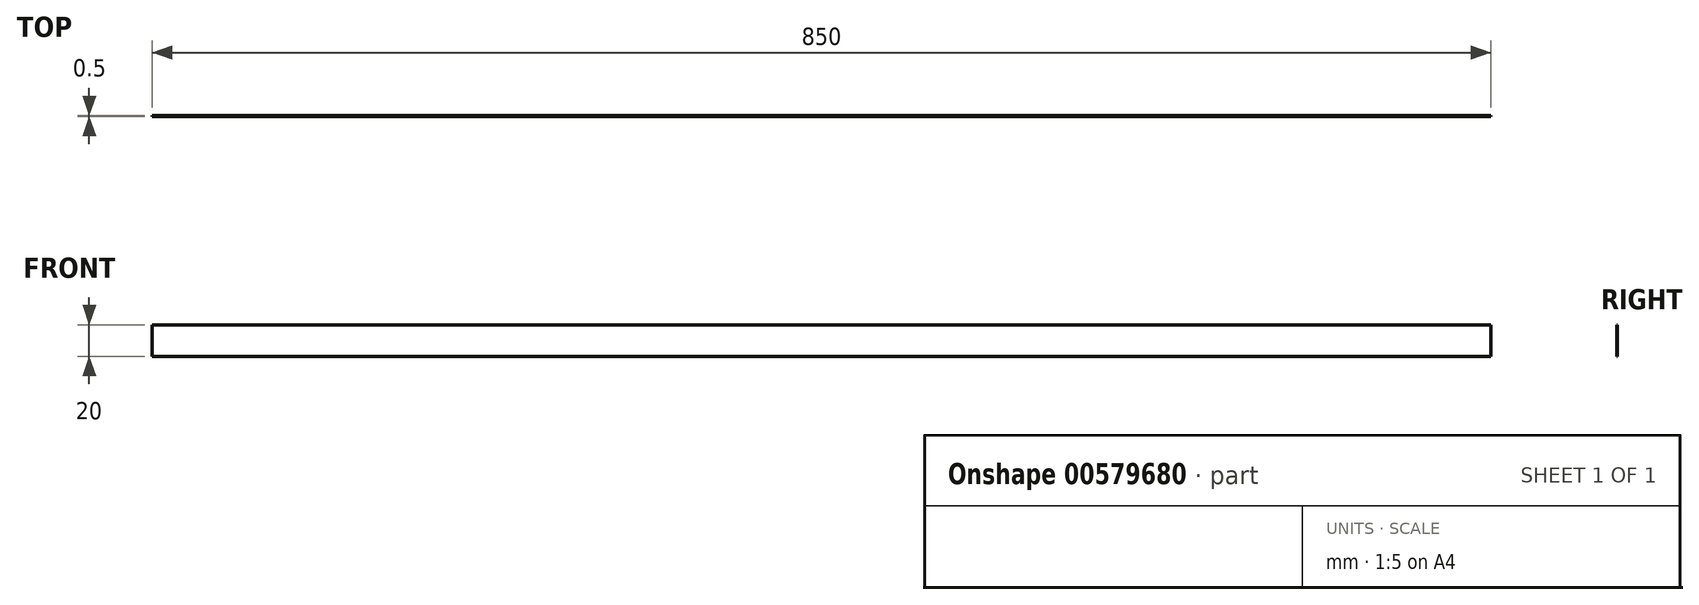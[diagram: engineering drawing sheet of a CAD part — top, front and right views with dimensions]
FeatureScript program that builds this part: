
annotation { "Feature Type Name" : "Feature", "Feature Type Description" : "" }
export const myFeature = defineFeature(function(context is Context, id is Id, definition is map)
    precondition{}
    {
        {
            var Q0;
            Q0=qCreatedBy(makeId("Front.planeOp"),FACE);
            var sketch = newSketch(context, id + "F0", { "sketchPlane" : qUnion([Q0])});
            skLineSegment(sketch, "E0", {"start": v(0, 34.2) * mm, "end": v(0, -45.96) * mm, "construction": true});
            skLineSegment(sketch, "E1.bottom", {"start": v(-425, 10) * mm, "end": v(425, 10) * mm});
            skLineSegment(sketch, "E1.top", {"start": v(-425, -10) * mm, "end": v(425, -10) * mm});
            skLineSegment(sketch, "E1.left", {"start": v(-425, 10) * mm, "end": v(-425, -10) * mm});
            skLineSegment(sketch, "E1.right", {"start": v(425, 10) * mm, "end": v(425, -10) * mm});
            skSolve(sketch);
        }
        {
            var Q0;
            Q0 = qSketchRegion(id + "F0", true);
            extrude(context, id + "F1", {"entities" : qUnion([Q0]), "depth" : 0.5 * mm, "offsetDistance" : 25 * mm});
        }
    });
